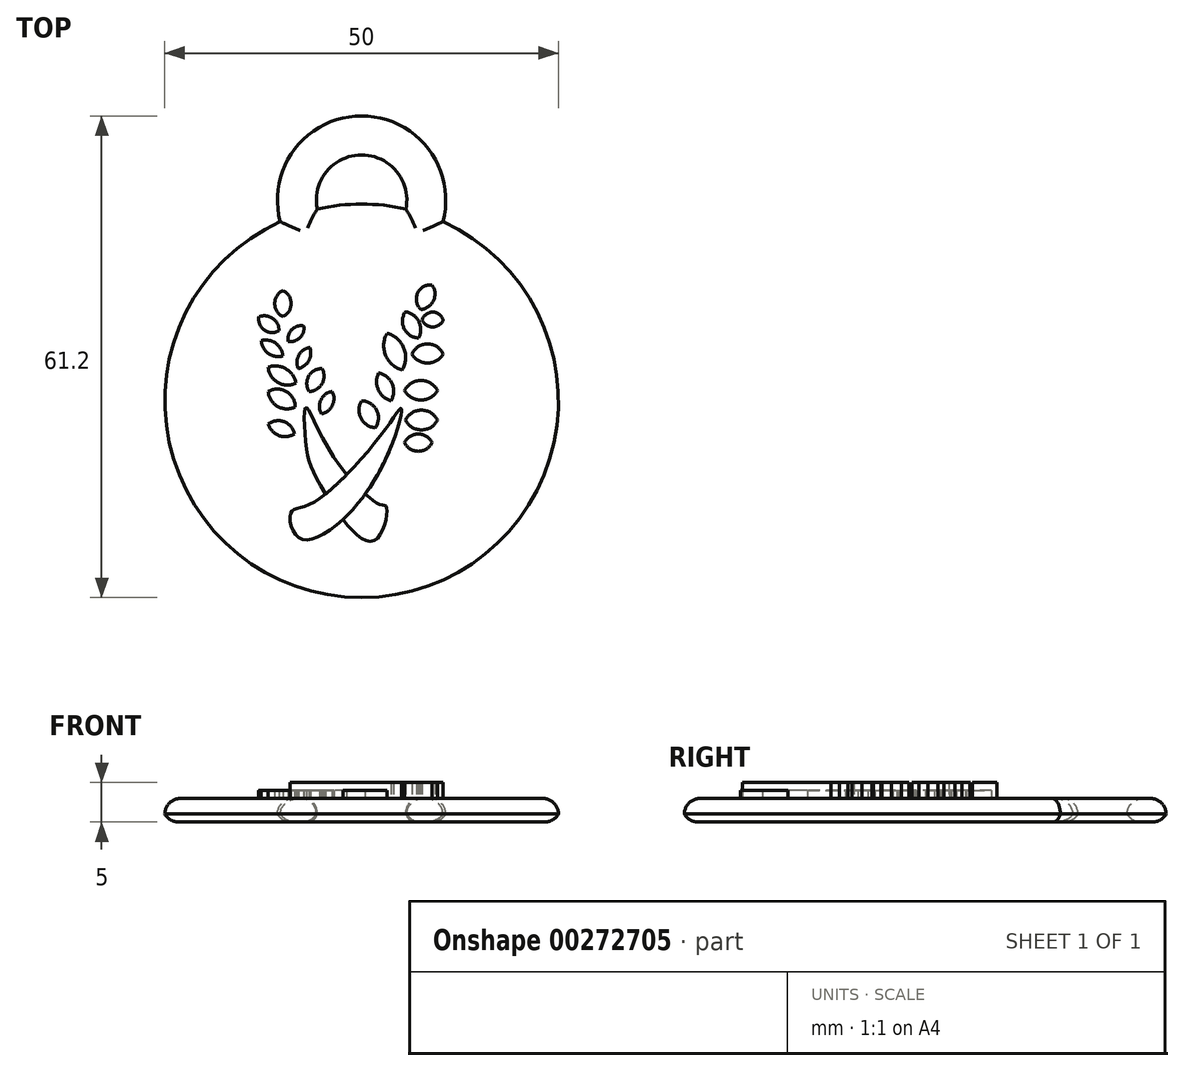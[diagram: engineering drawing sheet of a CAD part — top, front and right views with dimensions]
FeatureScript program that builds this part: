
annotation { "Feature Type Name" : "Feature", "Feature Type Description" : "" }
export const myFeature = defineFeature(function(context is Context, id is Id, definition is map)
    precondition{}
    {
        {
            var Q0;
            Q0=qCreatedBy(makeId("Top.planeOp"),FACE);
            var sketch = newSketch(context, id + "F0", { "sketchPlane" : qUnion([Q0])});
            skCircle(sketch, "E0", {"center": v(0, 0) * mm, "radius": 25 * mm});
            skSolve(sketch);
        }
        {
            var Q0;
            Q0=qCreatedBy(makeId("Top.planeOp"),FACE);
            var sketch = newSketch(context, id + "F1", { "sketchPlane" : qUnion([Q0])});
            skCircle(sketch, "E1", {"center": v(0, 25.5) * mm, "radius": 10.7 * mm});
            skCircle(sketch, "E2", {"center": v(0, 25.5) * mm, "radius": 5.74 * mm});
            skSolve(sketch);
        }
        {
            var Q0;
            Q0=makeQuery(id+"F1.imprint","IMPRINT",FACE,{"disambiguationData":[TD([[makeQuery(id+"F1.imprint","IMPRINT",EDGE,{"derivedFrom":sQuery(id+"F1.wireOp",EDGE,"E1")}),1.0]])]});
            var Q1;
            Q1=makeQuery(id+"F0.imprint","IMPRINT",FACE,{"disambiguationData":[TD([[makeQuery(id+"F0.imprint","IMPRINT",EDGE,{"derivedFrom":sQuery(id+"F0.wireOp",EDGE,"E0")}),1.0]])]});
            extrude(context, id + "F2", {"entities" : qUnion([Q0, Q1]), "depth" : 3 * mm});
        }
        {
            var Q0;
            Q0=makeQuery(id+"F2.opExtrude","CAP_FACE",FACE,{"disambiguationData":[OSD([sQuery(id+"F0.wireOp",EDGE,"E0")])],"isStart":false});
            var sketch = newSketch(context, id + "F3", { "sketchPlane" : qUnion([Q0])});
            skFitSpline(sketch, "E3", {"points": [v(3.19, -3.38) * mm, v(-6.58, -13.14) * mm, v(-8.97, -14.23) * mm, v(-7.77, -17.48) * mm, v(1.34, -10.54) * mm, v(5.03, -0.99) * mm, v(3.19, -3.38) * mm]});
            skFitSpline(sketch, "E4", {"points": [v(-7.12, -0.88) * mm, v(-7.01, -5.87) * mm, v(-5.28, -10.65) * mm, v(1.45, -17.8) * mm, v(3.19, -13.58) * mm, v(2.32, -13.14) * mm, v(-4.2, -6.09) * mm, v(-7.12, -0.88) * mm]});
            skSolve(sketch);
        }
        {
            var Q0;
            {var subQ0=sQuery(id+"F3.wireOp",EDGE,"E4");var subQ1=sQuery(id+"F3.wireOp",EDGE,"E3");var subQ2=makeQuery(id+"F3.imprint","INTERSECT",VERTEX,{"disambiguationData":[OD(1.0)],"derivedFrom":[subQ1,subQ0]});Q0=makeQuery(id+"F3.imprint","IMPRINT",FACE,{"disambiguationData":[TD([[makeQuery(id+"F3.imprint","IMPRINT",EDGE,{"disambiguationData":[TD([[subQ2,1.0]])],"derivedFrom":subQ1}),1.0]])]});}
            var Q1;
            {var subQ0=sQuery(id+"F3.wireOp",EDGE,"E4");var subQ1=sQuery(id+"F3.wireOp",EDGE,"E3");var subQ2=makeQuery(id+"F3.imprint","INTERSECT",VERTEX,{"disambiguationData":[OD(0.0)],"derivedFrom":[subQ1,subQ0]});Q1=makeQuery(id+"F3.imprint","IMPRINT",FACE,{"disambiguationData":[TD([[makeQuery(id+"F3.imprint","IMPRINT",EDGE,{"disambiguationData":[TD([[subQ2,1.0]])],"derivedFrom":subQ1}),1.0]])]});}
            var Q2;
            {var subQ0=sQuery(id+"F3.wireOp",EDGE,"E4");var subQ1=sQuery(id+"F3.wireOp",EDGE,"E3");var subQ2=makeQuery(id+"F3.imprint","INTERSECT",VERTEX,{"disambiguationData":[OD(0.0)],"derivedFrom":[subQ1,subQ0]});Q2=makeQuery(id+"F3.imprint","IMPRINT",FACE,{"disambiguationData":[TD([[makeQuery(id+"F3.imprint","IMPRINT",EDGE,{"disambiguationData":[TD([[subQ2,-1.0]])],"derivedFrom":subQ1}),1.0]])]});}
            extrude(context, id + "F4", {"entities" : qUnion([Q0, Q1, Q2]), "operationType" : NewBodyOperationType.ADD, "depth" : 2 * mm});
        }
        {
            var Q0;
            {var subQ0=sQuery(id+"F3.wireOp",EDGE,"E4");var subQ1=sQuery(id+"F3.wireOp",EDGE,"E3");var subQ2=makeQuery(id+"F3.imprint","INTERSECT",VERTEX,{"disambiguationData":[OD(0.0)],"derivedFrom":[subQ1,subQ0]});Q0=makeQuery(id+"F3.imprint","IMPRINT",FACE,{"disambiguationData":[TD([[makeQuery(id+"F3.imprint","IMPRINT",EDGE,{"disambiguationData":[TD([[subQ2,1.0]])],"derivedFrom":subQ1}),-1.0]])]});}
            var Q1;
            {var subQ0=sQuery(id+"F3.wireOp",EDGE,"E4");var subQ1=sQuery(id+"F3.wireOp",EDGE,"E3");var subQ2=makeQuery(id+"F3.imprint","INTERSECT",VERTEX,{"disambiguationData":[OD(2.0)],"derivedFrom":[subQ1,subQ0]});Q1=makeQuery(id+"F3.imprint","IMPRINT",FACE,{"disambiguationData":[TD([[makeQuery(id+"F3.imprint","IMPRINT",EDGE,{"disambiguationData":[TD([[subQ2,-1.0]])],"derivedFrom":subQ1}),-1.0]])]});}
            extrude(context, id + "F5", {"entities" : qUnion([Q0, Q1]), "operationType" : NewBodyOperationType.ADD, "depth" : 1 * mm});
        }
        {
            var Q0;
            Q0=makeQuery(id+"F2.opExtrude","CAP_FACE",FACE,{"disambiguationData":[OSD([sQuery(id+"F0.wireOp",EDGE,"E0")])],"isStart":false});
            var sketch = newSketch(context, id + "F6", { "sketchPlane" : qUnion([Q0])});
            skLineSegment(sketch, "E5", {"start": v(1.73, -3.44) * mm, "end": v(0, 0) * mm});
            skLineSegment(sketch, "E6", {"start": v(5.55, -2.44) * mm, "end": v(9.65, -2.44) * mm});
            skLineSegment(sketch, "E7", {"start": v(3.72, 0) * mm, "end": v(2.17, 3.54) * mm});
            skLineSegment(sketch, "E8", {"start": v(5.44, 1.33) * mm, "end": v(9.65, 1.33) * mm});
            skLineSegment(sketch, "E9", {"start": v(5.16, 3.93) * mm, "end": v(3.22, 8.58) * mm});
            skLineSegment(sketch, "E10", {"start": v(6.38, 5.92) * mm, "end": v(10.37, 5.92) * mm});
            skLineSegment(sketch, "E11", {"start": v(7.23, 7.99) * mm, "end": v(5.55, 11.31) * mm});
            skLineSegment(sketch, "E12", {"start": v(7.68, 10.25) * mm, "end": v(10.37, 10.25) * mm});
            skLineSegment(sketch, "E13", {"start": v(7.53, 11.61) * mm, "end": v(8.97, 14.71) * mm});
            skLineSegment(sketch, "E14", {"start": v(5.44, -5.3) * mm, "end": v(8.97, -5.3) * mm});
            skArc(sketch, "E15", {"start": v(1.73, -3.44) * mm, "mid": v(1.9, -1.2) * mm, "end": v(0, 0) * mm});
            skArc(sketch, "E16", {"start": v(0, 0) * mm, "mid": v(-0.08, -2.2) * mm, "end": v(1.73, -3.44) * mm});
            skArc(sketch, "E17", {"start": v(8.97, -5.3) * mm, "mid": v(7.2, -4.21) * mm, "end": v(5.44, -5.3) * mm});
            skArc(sketch, "E18", {"start": v(5.44, -5.3) * mm, "mid": v(7.2, -6.4) * mm, "end": v(8.97, -5.3) * mm});
            skArc(sketch, "E19", {"start": v(3.72, 0) * mm, "mid": v(3.87, 2.18) * mm, "end": v(2.17, 3.54) * mm});
            skArc(sketch, "E20", {"start": v(2.17, 3.54) * mm, "mid": v(2.11, 1.4) * mm, "end": v(3.72, 0) * mm});
            skArc(sketch, "E21", {"start": v(9.65, 1.33) * mm, "mid": v(7.54, 2.58) * mm, "end": v(5.44, 1.33) * mm});
            skArc(sketch, "E22", {"start": v(5.44, 1.33) * mm, "mid": v(7.54, 0.1) * mm, "end": v(9.65, 1.33) * mm});
            skArc(sketch, "E23", {"start": v(3.22, 8.58) * mm, "mid": v(3.06, 5.78) * mm, "end": v(5.16, 3.93) * mm});
            skArc(sketch, "E24", {"start": v(5.16, 3.93) * mm, "mid": v(5.35, 6.74) * mm, "end": v(3.22, 8.58) * mm});
            skArc(sketch, "E25", {"start": v(10.37, 5.92) * mm, "mid": v(8.37, 7.24) * mm, "end": v(6.38, 5.92) * mm});
            skArc(sketch, "E26", {"start": v(6.38, 5.92) * mm, "mid": v(8.37, 4.8) * mm, "end": v(10.37, 5.92) * mm});
            skArc(sketch, "E27", {"start": v(5.55, 11.31) * mm, "mid": v(5.41, 9.16) * mm, "end": v(7.23, 7.99) * mm});
            skArc(sketch, "E28", {"start": v(7.23, 7.99) * mm, "mid": v(7.27, 10.1) * mm, "end": v(5.55, 11.31) * mm});
            skArc(sketch, "E29", {"start": v(10.37, 10.25) * mm, "mid": v(9.03, 11.27) * mm, "end": v(7.68, 10.25) * mm});
            skArc(sketch, "E30", {"start": v(7.68, 10.25) * mm, "mid": v(9.03, 9.38) * mm, "end": v(10.37, 10.25) * mm});
            skArc(sketch, "E31", {"start": v(8.97, 14.71) * mm, "mid": v(7.12, 13.69) * mm, "end": v(7.53, 11.61) * mm});
            skArc(sketch, "E32", {"start": v(7.53, 11.61) * mm, "mid": v(9.14, 12.75) * mm, "end": v(8.97, 14.71) * mm});
            skArc(sketch, "E33", {"start": v(9.65, -2.44) * mm, "mid": v(7.6, -1.19) * mm, "end": v(5.55, -2.44) * mm});
            skArc(sketch, "E34", {"start": v(5.55, -2.44) * mm, "mid": v(7.6, -3.7) * mm, "end": v(9.65, -2.44) * mm});
            skSolve(sketch);
        }
        {
            var Q0;
            Q0=makeQuery(id+"F6.imprint","IMPRINT",FACE,{"disambiguationData":[TD([[makeQuery(id+"F6.imprint","IMPRINT",EDGE,{"derivedFrom":sQuery(id+"F6.wireOp",EDGE,"E5")}),-1.0]])]});
            var Q1;
            Q1=makeQuery(id+"F6.imprint","IMPRINT",FACE,{"disambiguationData":[TD([[makeQuery(id+"F6.imprint","IMPRINT",EDGE,{"derivedFrom":sQuery(id+"F6.wireOp",EDGE,"E5")}),1.0]])]});
            var Q2;
            Q2=makeQuery(id+"F6.imprint","IMPRINT",FACE,{"disambiguationData":[TD([[makeQuery(id+"F6.imprint","IMPRINT",EDGE,{"derivedFrom":sQuery(id+"F6.wireOp",EDGE,"E14")}),-1.0]])]});
            var Q3;
            Q3=makeQuery(id+"F6.imprint","IMPRINT",FACE,{"disambiguationData":[TD([[makeQuery(id+"F6.imprint","IMPRINT",EDGE,{"derivedFrom":sQuery(id+"F6.wireOp",EDGE,"E14")}),1.0]])]});
            var Q4;
            Q4=makeQuery(id+"F6.imprint","IMPRINT",FACE,{"disambiguationData":[TD([[makeQuery(id+"F6.imprint","IMPRINT",EDGE,{"derivedFrom":sQuery(id+"F6.wireOp",EDGE,"E6")}),-1.0]])]});
            var Q5;
            Q5=makeQuery(id+"F6.imprint","IMPRINT",FACE,{"disambiguationData":[TD([[makeQuery(id+"F6.imprint","IMPRINT",EDGE,{"derivedFrom":sQuery(id+"F6.wireOp",EDGE,"E6")}),1.0]])]});
            var Q6;
            Q6=makeQuery(id+"F6.imprint","IMPRINT",FACE,{"disambiguationData":[TD([[makeQuery(id+"F6.imprint","IMPRINT",EDGE,{"derivedFrom":sQuery(id+"F6.wireOp",EDGE,"E7")}),-1.0]])]});
            var Q7;
            Q7=makeQuery(id+"F6.imprint","IMPRINT",FACE,{"disambiguationData":[TD([[makeQuery(id+"F6.imprint","IMPRINT",EDGE,{"derivedFrom":sQuery(id+"F6.wireOp",EDGE,"E7")}),1.0]])]});
            var Q8;
            Q8=makeQuery(id+"F6.imprint","IMPRINT",FACE,{"disambiguationData":[TD([[makeQuery(id+"F6.imprint","IMPRINT",EDGE,{"derivedFrom":sQuery(id+"F6.wireOp",EDGE,"E8")}),1.0]])]});
            var Q9;
            Q9=makeQuery(id+"F6.imprint","IMPRINT",FACE,{"disambiguationData":[TD([[makeQuery(id+"F6.imprint","IMPRINT",EDGE,{"derivedFrom":sQuery(id+"F6.wireOp",EDGE,"E8")}),-1.0]])]});
            var Q10;
            Q10=makeQuery(id+"F6.imprint","IMPRINT",FACE,{"disambiguationData":[TD([[makeQuery(id+"F6.imprint","IMPRINT",EDGE,{"derivedFrom":sQuery(id+"F6.wireOp",EDGE,"E9")}),-1.0]])]});
            var Q11;
            Q11=makeQuery(id+"F6.imprint","IMPRINT",FACE,{"disambiguationData":[TD([[makeQuery(id+"F6.imprint","IMPRINT",EDGE,{"derivedFrom":sQuery(id+"F6.wireOp",EDGE,"E9")}),1.0]])]});
            var Q12;
            Q12=makeQuery(id+"F6.imprint","IMPRINT",FACE,{"disambiguationData":[TD([[makeQuery(id+"F6.imprint","IMPRINT",EDGE,{"derivedFrom":sQuery(id+"F6.wireOp",EDGE,"E10")}),1.0]])]});
            var Q13;
            Q13=makeQuery(id+"F6.imprint","IMPRINT",FACE,{"disambiguationData":[TD([[makeQuery(id+"F6.imprint","IMPRINT",EDGE,{"derivedFrom":sQuery(id+"F6.wireOp",EDGE,"E10")}),-1.0]])]});
            var Q14;
            Q14=makeQuery(id+"F6.imprint","IMPRINT",FACE,{"disambiguationData":[TD([[makeQuery(id+"F6.imprint","IMPRINT",EDGE,{"derivedFrom":sQuery(id+"F6.wireOp",EDGE,"E11")}),-1.0]])]});
            var Q15;
            Q15=makeQuery(id+"F6.imprint","IMPRINT",FACE,{"disambiguationData":[TD([[makeQuery(id+"F6.imprint","IMPRINT",EDGE,{"derivedFrom":sQuery(id+"F6.wireOp",EDGE,"E11")}),1.0]])]});
            var Q16;
            Q16=makeQuery(id+"F6.imprint","IMPRINT",FACE,{"disambiguationData":[TD([[makeQuery(id+"F6.imprint","IMPRINT",EDGE,{"derivedFrom":sQuery(id+"F6.wireOp",EDGE,"E12")}),1.0]])]});
            var Q17;
            Q17=makeQuery(id+"F6.imprint","IMPRINT",FACE,{"disambiguationData":[TD([[makeQuery(id+"F6.imprint","IMPRINT",EDGE,{"derivedFrom":sQuery(id+"F6.wireOp",EDGE,"E12")}),-1.0]])]});
            var Q18;
            Q18=makeQuery(id+"F6.imprint","IMPRINT",FACE,{"disambiguationData":[TD([[makeQuery(id+"F6.imprint","IMPRINT",EDGE,{"derivedFrom":sQuery(id+"F6.wireOp",EDGE,"E13")}),-1.0]])]});
            var Q19;
            Q19=makeQuery(id+"F6.imprint","IMPRINT",FACE,{"disambiguationData":[TD([[makeQuery(id+"F6.imprint","IMPRINT",EDGE,{"derivedFrom":sQuery(id+"F6.wireOp",EDGE,"E13")}),1.0]])]});
            extrude(context, id + "F7", {"entities" : qUnion([Q0, Q1, Q2, Q3, Q4, Q5, Q6, Q7, Q8, Q9, Q10, Q11, Q12, Q13, Q14, Q15, Q16, Q17, Q18, Q19]), "operationType" : NewBodyOperationType.ADD, "depth" : 2 * mm});
        }
        {
            var Q0;
            Q0=makeQuery(id+"F2.opExtrude","CAP_FACE",FACE,{"disambiguationData":[OSD([sQuery(id+"F0.wireOp",EDGE,"E0")])],"isStart":false});
            var sketch = newSketch(context, id + "F8", { "sketchPlane" : qUnion([Q0])});
            skLineSegment(sketch, "E35", {"start": v(-8.53, -4.2) * mm, "end": v(-11.86, -2.93) * mm});
            skLineSegment(sketch, "E36", {"start": v(-5.1, -1.65) * mm, "end": v(-3.73, 1.19) * mm});
            skLineSegment(sketch, "E37", {"start": v(-8.43, -0.77) * mm, "end": v(-11.86, 1.19) * mm});
            skLineSegment(sketch, "E38", {"start": v(-6.67, 1.19) * mm, "end": v(-5.01, 4.1) * mm});
            skLineSegment(sketch, "E39", {"start": v(-8.33, 2.27) * mm, "end": v(-11.86, 4.28) * mm});
            skLineSegment(sketch, "E40", {"start": v(-8.04, 4.1) * mm, "end": v(-6.57, 6.77) * mm});
            skLineSegment(sketch, "E41", {"start": v(-10, 5.7) * mm, "end": v(-12.74, 7.66) * mm});
            skLineSegment(sketch, "E42", {"start": v(-9.31, 7.56) * mm, "end": v(-7.35, 9.52) * mm});
            skLineSegment(sketch, "E43", {"start": v(-10.5, 8.93) * mm, "end": v(-13.04, 10.7) * mm});
            skLineSegment(sketch, "E44", {"start": v(-10, 10.7) * mm, "end": v(-10, 14.02) * mm});
            skArc(sketch, "E45", {"start": v(-8.53, -4.2) * mm, "mid": v(-9.85, -2.65) * mm, "end": v(-11.86, -2.93) * mm});
            skArc(sketch, "E46", {"start": v(-11.86, -2.93) * mm, "mid": v(-10.52, -4.4) * mm, "end": v(-8.53, -4.2) * mm});
            skArc(sketch, "E47", {"start": v(-8.43, -0.77) * mm, "mid": v(-9.58, 1.2) * mm, "end": v(-11.86, 1.19) * mm});
            skArc(sketch, "E48", {"start": v(-11.86, 1.19) * mm, "mid": v(-10.67, -0.7) * mm, "end": v(-8.43, -0.77) * mm});
            skArc(sketch, "E49", {"start": v(-3.73, 1.19) * mm, "mid": v(-5.17, 0.13) * mm, "end": v(-5.1, -1.65) * mm});
            skArc(sketch, "E50", {"start": v(-5.1, -1.65) * mm, "mid": v(-3.7, -0.57) * mm, "end": v(-3.73, 1.19) * mm});
            skArc(sketch, "E51", {"start": v(-5.01, 4.1) * mm, "mid": v(-6.72, 3.14) * mm, "end": v(-6.67, 1.19) * mm});
            skArc(sketch, "E52", {"start": v(-6.67, 1.19) * mm, "mid": v(-5.03, 2.18) * mm, "end": v(-5.01, 4.1) * mm});
            skArc(sketch, "E53", {"start": v(-11.86, 4.28) * mm, "mid": v(-10.64, 2.33) * mm, "end": v(-8.33, 2.27) * mm});
            skArc(sketch, "E54", {"start": v(-8.33, 2.27) * mm, "mid": v(-9.64, 4.08) * mm, "end": v(-11.86, 4.28) * mm});
            skArc(sketch, "E55", {"start": v(-6.57, 6.77) * mm, "mid": v(-7.98, 5.8) * mm, "end": v(-8.04, 4.1) * mm});
            skArc(sketch, "E56", {"start": v(-8.04, 4.1) * mm, "mid": v(-6.7, 5.1) * mm, "end": v(-6.57, 6.77) * mm});
            skArc(sketch, "E57", {"start": v(-12.74, 7.66) * mm, "mid": v(-11.85, 6) * mm, "end": v(-10, 5.7) * mm});
            skArc(sketch, "E58", {"start": v(-10, 5.7) * mm, "mid": v(-10.92, 7.32) * mm, "end": v(-12.74, 7.66) * mm});
            skArc(sketch, "E59", {"start": v(-7.35, 9.52) * mm, "mid": v(-8.86, 9.06) * mm, "end": v(-9.31, 7.56) * mm});
            skArc(sketch, "E60", {"start": v(-9.31, 7.56) * mm, "mid": v(-7.82, 8.03) * mm, "end": v(-7.35, 9.52) * mm});
            skArc(sketch, "E61", {"start": v(-13.04, 10.7) * mm, "mid": v(-12.34, 8.97) * mm, "end": v(-10.5, 8.93) * mm});
            skArc(sketch, "E62", {"start": v(-10.5, 8.93) * mm, "mid": v(-11.3, 10.48) * mm, "end": v(-13.04, 10.7) * mm});
            skArc(sketch, "E63", {"start": v(-10, 14.02) * mm, "mid": v(-11.04, 12.36) * mm, "end": v(-10, 10.7) * mm});
            skArc(sketch, "E64", {"start": v(-10, 10.7) * mm, "mid": v(-8.95, 12.36) * mm, "end": v(-10, 14.02) * mm});
            skSolve(sketch);
        }
        {
            var Q0;
            Q0=makeQuery(id+"F8.imprint","IMPRINT",FACE,{"disambiguationData":[TD([[makeQuery(id+"F8.imprint","IMPRINT",EDGE,{"derivedFrom":sQuery(id+"F8.wireOp",EDGE,"E35")}),-1.0]])]});
            var Q1;
            Q1=makeQuery(id+"F8.imprint","IMPRINT",FACE,{"disambiguationData":[TD([[makeQuery(id+"F8.imprint","IMPRINT",EDGE,{"derivedFrom":sQuery(id+"F8.wireOp",EDGE,"E35")}),1.0]])]});
            var Q2;
            Q2=makeQuery(id+"F8.imprint","IMPRINT",FACE,{"disambiguationData":[TD([[makeQuery(id+"F8.imprint","IMPRINT",EDGE,{"derivedFrom":sQuery(id+"F8.wireOp",EDGE,"E36")}),-1.0]])]});
            var Q3;
            Q3=makeQuery(id+"F8.imprint","IMPRINT",FACE,{"disambiguationData":[TD([[makeQuery(id+"F8.imprint","IMPRINT",EDGE,{"derivedFrom":sQuery(id+"F8.wireOp",EDGE,"E36")}),1.0]])]});
            var Q4;
            Q4=makeQuery(id+"F8.imprint","IMPRINT",FACE,{"disambiguationData":[TD([[makeQuery(id+"F8.imprint","IMPRINT",EDGE,{"derivedFrom":sQuery(id+"F8.wireOp",EDGE,"E38")}),-1.0]])]});
            var Q5;
            Q5=makeQuery(id+"F8.imprint","IMPRINT",FACE,{"disambiguationData":[TD([[makeQuery(id+"F8.imprint","IMPRINT",EDGE,{"derivedFrom":sQuery(id+"F8.wireOp",EDGE,"E38")}),1.0]])]});
            var Q6;
            Q6=makeQuery(id+"F8.imprint","IMPRINT",FACE,{"disambiguationData":[TD([[makeQuery(id+"F8.imprint","IMPRINT",EDGE,{"derivedFrom":sQuery(id+"F8.wireOp",EDGE,"E37")}),-1.0]])]});
            var Q7;
            Q7=makeQuery(id+"F8.imprint","IMPRINT",FACE,{"disambiguationData":[TD([[makeQuery(id+"F8.imprint","IMPRINT",EDGE,{"derivedFrom":sQuery(id+"F8.wireOp",EDGE,"E37")}),1.0]])]});
            var Q8;
            Q8=makeQuery(id+"F8.imprint","IMPRINT",FACE,{"disambiguationData":[TD([[makeQuery(id+"F8.imprint","IMPRINT",EDGE,{"derivedFrom":sQuery(id+"F8.wireOp",EDGE,"E39")}),1.0]])]});
            var Q9;
            Q9=makeQuery(id+"F8.imprint","IMPRINT",FACE,{"disambiguationData":[TD([[makeQuery(id+"F8.imprint","IMPRINT",EDGE,{"derivedFrom":sQuery(id+"F8.wireOp",EDGE,"E39")}),-1.0]])]});
            var Q10;
            Q10=makeQuery(id+"F8.imprint","IMPRINT",FACE,{"disambiguationData":[TD([[makeQuery(id+"F8.imprint","IMPRINT",EDGE,{"derivedFrom":sQuery(id+"F8.wireOp",EDGE,"E40")}),1.0]])]});
            var Q11;
            Q11=makeQuery(id+"F8.imprint","IMPRINT",FACE,{"disambiguationData":[TD([[makeQuery(id+"F8.imprint","IMPRINT",EDGE,{"derivedFrom":sQuery(id+"F8.wireOp",EDGE,"E40")}),-1.0]])]});
            var Q12;
            Q12=makeQuery(id+"F8.imprint","IMPRINT",FACE,{"disambiguationData":[TD([[makeQuery(id+"F8.imprint","IMPRINT",EDGE,{"derivedFrom":sQuery(id+"F8.wireOp",EDGE,"E41")}),-1.0]])]});
            var Q13;
            Q13=makeQuery(id+"F8.imprint","IMPRINT",FACE,{"disambiguationData":[TD([[makeQuery(id+"F8.imprint","IMPRINT",EDGE,{"derivedFrom":sQuery(id+"F8.wireOp",EDGE,"E41")}),1.0]])]});
            var Q14;
            Q14=makeQuery(id+"F8.imprint","IMPRINT",FACE,{"disambiguationData":[TD([[makeQuery(id+"F8.imprint","IMPRINT",EDGE,{"derivedFrom":sQuery(id+"F8.wireOp",EDGE,"E42")}),1.0]])]});
            var Q15;
            Q15=makeQuery(id+"F8.imprint","IMPRINT",FACE,{"disambiguationData":[TD([[makeQuery(id+"F8.imprint","IMPRINT",EDGE,{"derivedFrom":sQuery(id+"F8.wireOp",EDGE,"E42")}),-1.0]])]});
            var Q16;
            Q16=makeQuery(id+"F8.imprint","IMPRINT",FACE,{"disambiguationData":[TD([[makeQuery(id+"F8.imprint","IMPRINT",EDGE,{"derivedFrom":sQuery(id+"F8.wireOp",EDGE,"E43")}),-1.0]])]});
            var Q17;
            Q17=makeQuery(id+"F8.imprint","IMPRINT",FACE,{"disambiguationData":[TD([[makeQuery(id+"F8.imprint","IMPRINT",EDGE,{"derivedFrom":sQuery(id+"F8.wireOp",EDGE,"E43")}),1.0]])]});
            var Q18;
            Q18=makeQuery(id+"F8.imprint","IMPRINT",FACE,{"disambiguationData":[TD([[makeQuery(id+"F8.imprint","IMPRINT",EDGE,{"derivedFrom":sQuery(id+"F8.wireOp",EDGE,"E44")}),1.0]])]});
            var Q19;
            Q19=makeQuery(id+"F8.imprint","IMPRINT",FACE,{"disambiguationData":[TD([[makeQuery(id+"F8.imprint","IMPRINT",EDGE,{"derivedFrom":sQuery(id+"F8.wireOp",EDGE,"E44")}),-1.0]])]});
            extrude(context, id + "F9", {"entities" : qUnion([Q0, Q1, Q2, Q3, Q4, Q5, Q6, Q7, Q8, Q9, Q10, Q11, Q12, Q13, Q14, Q15, Q16, Q17, Q18, Q19]), "operationType" : NewBodyOperationType.ADD, "depth" : 1 * mm});
        }
        {
            var Q0;
            Q0=makeQuery(id+"F2.opExtrude","SWEPT_BODY",BODY,{"disambiguationData":[OSD([sQuery(id+"F0.wireOp",EDGE,"E0")])]});
            var Q1;
            Q1=makeQuery(id+"F2.opExtrude","SWEPT_BODY",BODY,{"disambiguationData":[OSD([sQuery(id+"F1.wireOp",EDGE,"E1"),sQuery(id+"F1.wireOp",EDGE,"E2")])]});
            booleanBodies(context, id + "F10", {"operationType" : BooleanOperationType.UNION, "tools" : qUnion([Q0, Q1])});
        }
        {
            var Q0;
            {var subQ0=sQuery(id+"F0.wireOp",EDGE,"E0");var subQ1=sQuery(id+"F1.wireOp",EDGE,"E1");Q0=makeQuery(id+"F10.opBoolean","SPLIT",EDGE,{"disambiguationData":[TD([makeQuery(id+"F2.opExtrude","SWEPT_FACE",FACE,{"disambiguationData":[OSD([subQ1])]})])],"derivedFrom":makeQuery(id+"F2.opExtrude","CAP_EDGE",EDGE,{"disambiguationData":[OSD([subQ0])],"isStart":false})});}
            var Q1;
            Q1=makeQuery(id+"F2.opExtrude","CAP_EDGE",EDGE,{"disambiguationData":[OSD([sQuery(id+"F1.wireOp",EDGE,"E1")])],"isStart":false});
            var Q2;
            Q2=makeQuery(id+"F2.opExtrude","CAP_EDGE",EDGE,{"disambiguationData":[OSD([sQuery(id+"F1.wireOp",EDGE,"E2")])],"isStart":false});
            var Q3;
            {var subQ0=sQuery(id+"F0.wireOp",EDGE,"E0");var subQ1=sQuery(id+"F1.wireOp",EDGE,"E2");Q3=makeQuery(id+"F10.opBoolean","SPLIT",EDGE,{"disambiguationData":[TD([makeQuery(id+"F2.opExtrude","SWEPT_FACE",FACE,{"disambiguationData":[OSD([subQ1])]})])],"derivedFrom":makeQuery(id+"F2.opExtrude","CAP_EDGE",EDGE,{"disambiguationData":[OSD([subQ0])],"isStart":false})});}
            fillet(context, id + "F11", {"entities" : qUnion([Q0, Q1, Q2, Q3]), "radius" : 2 * mm, "tangentPropagation" : true, "allowEdgeOverflow" : false});
        }
        {
            var Q0;
            {var subQ0=sQuery(id+"F0.wireOp",EDGE,"E0");var subQ1=sQuery(id+"F1.wireOp",EDGE,"E1");Q0=makeQuery(id+"F10.opBoolean","SPLIT",EDGE,{"disambiguationData":[TD([makeQuery(id+"F2.opExtrude","SWEPT_FACE",FACE,{"disambiguationData":[OSD([subQ1])]})])],"derivedFrom":makeQuery(id+"F2.opExtrude","CAP_EDGE",EDGE,{"disambiguationData":[OSD([subQ0])],"isStart":true})});}
            var Q1;
            Q1=makeQuery(id+"F2.opExtrude","CAP_EDGE",EDGE,{"disambiguationData":[OSD([sQuery(id+"F1.wireOp",EDGE,"E1")])],"isStart":true});
            var Q2;
            Q2=makeQuery(id+"F2.opExtrude","CAP_EDGE",EDGE,{"disambiguationData":[OSD([sQuery(id+"F1.wireOp",EDGE,"E2")])],"isStart":true});
            var Q3;
            {var subQ0=sQuery(id+"F0.wireOp",EDGE,"E0");var subQ1=sQuery(id+"F1.wireOp",EDGE,"E2");Q3=makeQuery(id+"F10.opBoolean","SPLIT",EDGE,{"disambiguationData":[TD([makeQuery(id+"F2.opExtrude","SWEPT_FACE",FACE,{"disambiguationData":[OSD([subQ1])]})])],"derivedFrom":makeQuery(id+"F2.opExtrude","CAP_EDGE",EDGE,{"disambiguationData":[OSD([subQ0])],"isStart":true})});}
            fillet(context, id + "F12", {"entities" : qUnion([Q0, Q1, Q2, Q3]), "radius" : 2 * mm, "tangentPropagation" : true, "allowEdgeOverflow" : false});
        }
    });
